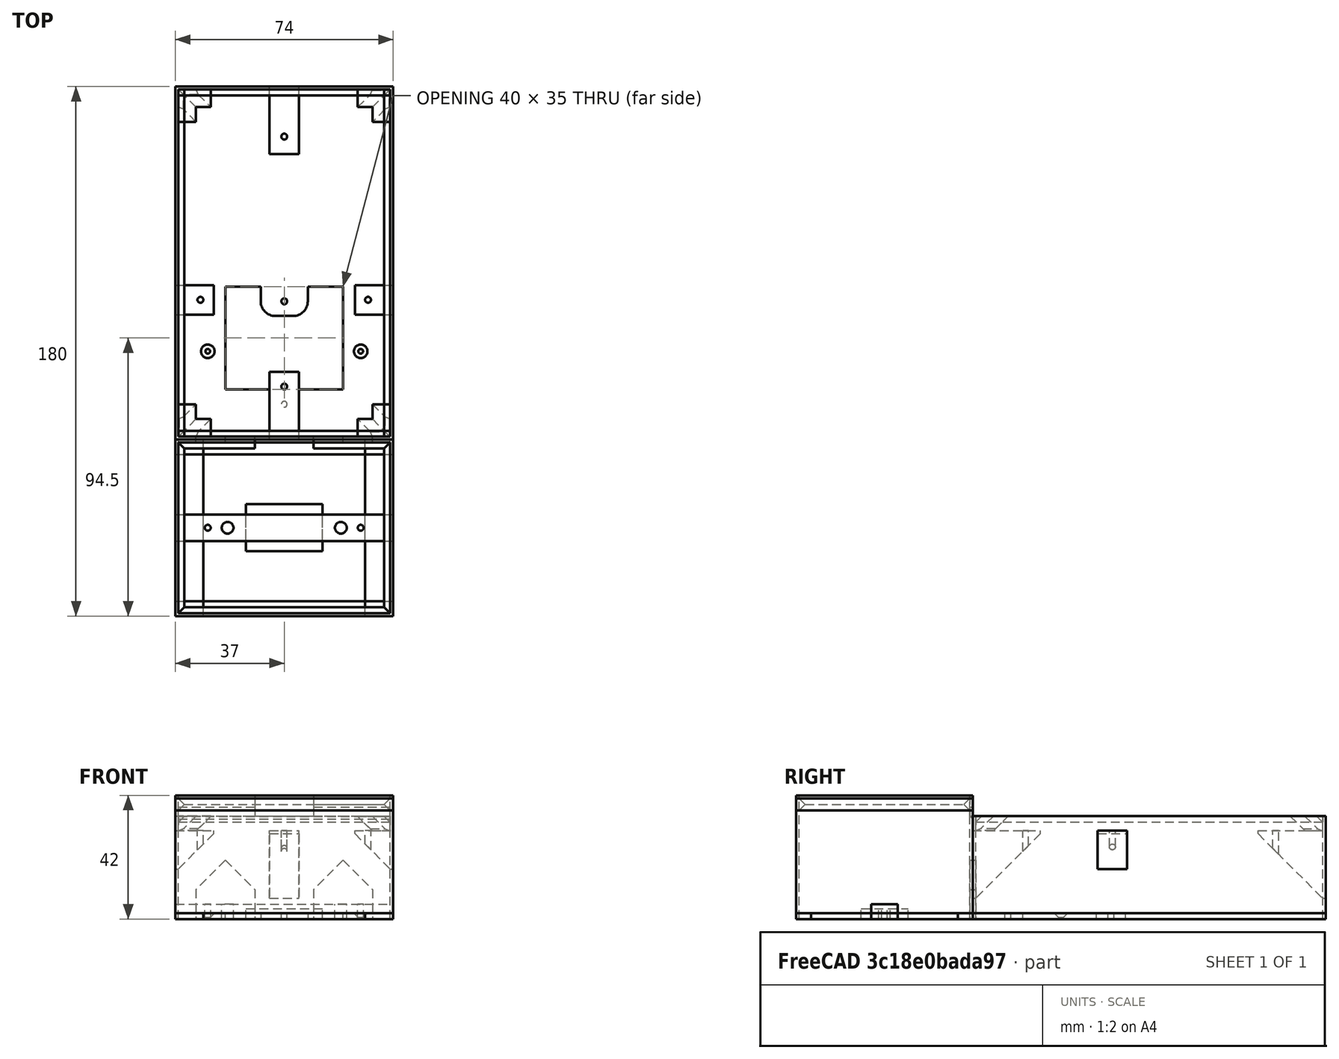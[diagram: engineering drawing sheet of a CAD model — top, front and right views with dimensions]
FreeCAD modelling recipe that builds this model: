
FCSTD DOCUMENT  (FreeCAD 0.16R)
Label: sonoff-T1-US-aufputz-und-Steckdose_v2.3
License: All rights reserved
LicenseURL: http://en.wikipedia.org/wiki/All_rights_reserved
objects: Part::Box×37, Part::Cut×30, Part::Chamfer×24, Part::Cylinder×12, Part::Fillet×1
note: 104 computed .brp shape members not serialized (recipe doc carries the construction recipe); baked Part::Feature solids carry a one-line shape summary decoded from their .brp

FEATURE [Part::Box] Box028  label="Cube023"
  Height = 2
  Length = 72
  Placement = pos=(1,1,33) rot=(0,0,1;0rad)
  Width = 2
FEATURE [Part::Chamfer] Chamfer009
  Base = -> Box028
  Edges = 1 edges r=1.99: [Edge11]
FEATURE [Part::Box] Box037  label="Cube028"
  Height = 3.5
  Length = 26
  Placement = pos=(24,-38,0) rot=(0,0,1;0rad)
  Width = 16
FEATURE [Part::Cylinder] Cylinder
  Angle = 360
  Height = 10
  Placement = pos=(17.75,-30,0) rot=(0,0,1;0rad)
  Radius = 2
FEATURE [Part::Cylinder] Cylinder001
  Angle = 360
  Height = 10
  Placement = pos=(56.25,-30,0) rot=(0,0,1;0rad)
  Radius = 2
FEATURE [Part::Box] Box038  label="Kragen Stecker"
  Height = 4.1
  Length = 74
  Placement = pos=(0,-60,0) rot=(0,0,1;0rad)
  Width = 60
FEATURE [Part::Box] Box039  label="Kragen Stecker Ausschnitt"
  Height = 4.1
  Length = 68
  Placement = pos=(3,-57,0) rot=(0,0,1;0rad)
  Width = 54
FEATURE [Part::Cut] Cut019
  Base = -> Box038
  Placement = pos=(0,0,36.9) rot=(0,0,1;0rad)
  Tool = -> Box039
FEATURE [Part::Chamfer] Chamfer021
  Base = -> Cut019
  Edges = 4 edges r=2: [Edge10,Edge11,Edge12,Edge13]
FEATURE [Part::Chamfer] Chamfer022  label="Kragen"
  Base = -> Chamfer021
  Edges = 4 edges r=2: [Edge26,Edge29,Edge31,Edge32]
FEATURE [Part::Box] Box045  label="Cube034"
  Height = 4
  Length = 72
  Placement = pos=(1,-1,34) rot=(0,0,1;0rad)
  Width = 1
FEATURE [Part::Chamfer] Chamfer027  label="Verstärkung"
  Base = -> Box045
  Edges = 1 edges r=0.99: [Edge9]
FEATURE [Part::Box] Box032  label="Basis Stecker"
  Height = 42
  Length = 74
  Placement = pos=(0,-60,0) rot=(0,0,1;0rad)
  Width = 60
FEATURE [Part::Box] Box033  label="Ausschnitt Stecker"
  Height = 42
  Length = 72
  Placement = pos=(1,-59,0) rot=(0,0,1;0rad)
  Width = 58
FEATURE [Part::Cut] Cut014
  Base = -> Box032
  Tool = -> Box033
FEATURE [Part::Box] Box  label="Basis"
  Height = 35
  Length = 74
  Width = 120
FEATURE [Part::Box] Box001  label="Ausschnitt"
  Height = 35
  Length = 72
  Placement = pos=(1,1,0) rot=(0,0,1;0rad)
  Width = 118
FEATURE [Part::Cut] Cut
  Base = -> Box
  Tool = -> Box001
FEATURE [Part::Box] Box014  label="Basis001"
  Height = 2
  Length = 74
  Width = 120
FEATURE [Part::Box] Box024  label="Cube019"
  Height = 5
  Length = 5
  Placement = pos=(63,109,30) rot=(0,0,1;0rad)
  Width = 5
FEATURE [Part::Box] Box025  label="Cube020"
  Height = 5
  Length = 11
  Placement = pos=(63,109,30) rot=(0,0,1;0rad)
  Width = 11
FEATURE [Part::Cut] Cut012
  Base = -> Box025
  Tool = -> Box024
FEATURE [Part::Chamfer] Chamfer004
  Base = -> Cut012
  Edges = 4 edges r=4.9: [Edge4,Edge5,Edge15,Edge16]
  Placement = pos=(-1,-1,0) rot=(0,0,1;0rad)
FEATURE [Part::Box] Box046  label="Cube035"
  Height = 2
  Length = 72
  Placement = pos=(1,1,33) rot=(0,0,1;0rad)
  Width = 2
FEATURE [Part::Box] Box029  label="Cube024"
  Height = 2
  Length = 2
  Placement = pos=(1,1,33) rot=(0,0,1;0rad)
  Width = 118
FEATURE [Part::Box] Box030  label="Cube025"
  Height = 2
  Length = 72
  Placement = pos=(1,117,33) rot=(0,0,1;0rad)
  Width = 2
FEATURE [Part::Box] Box031  label="Cube026"
  Height = 2
  Length = 2
  Placement = pos=(71,1,33) rot=(0,0,1;0rad)
  Width = 118
FEATURE [Part::Chamfer] Chamfer008
  Base = -> Box031
  Edges = 1 edges r=1.9: [Edge4]
FEATURE [Part::Chamfer] Chamfer028
  Base = -> Box030
  Edges = 1 edges r=1.9: [Edge9]
FEATURE [Part::Chamfer] Chamfer010
  Base = -> Box029
  Edges = 1 edges r=1.9: [Edge8]
FEATURE [Part::Chamfer] Chamfer011
  Base = -> Box046
  Edges = 1 edges r=1.9: [Edge11]
FEATURE [Part::Box] Box047  label="Cube036"
  Height = 5
  Length = 11
  Placement = pos=(63,109,30) rot=(0,0,1;0rad)
  Width = 11
FEATURE [Part::Box] Box048  label="Cube037"
  Height = 5
  Length = 5
  Placement = pos=(63,109,30) rot=(0,0,1;0rad)
  Width = 5
FEATURE [Part::Cut] Cut013
  Base = -> Box047
  Tool = -> Box048
FEATURE [Part::Chamfer] Chamfer012
  Base = -> Cut013
  Edges = 4 edges r=4.9: [Edge4,Edge5,Edge15,Edge16]
  Placement = pos=(121,45,0) rot=(0,0,1;1.5708rad)
FEATURE [Part::Chamfer] Chamfer013
  Base = -> Chamfer004
  Edges = 2 edges r=0.9: [Edge19,Edge23]
FEATURE [Part::Chamfer] Chamfer014
  Base = -> Chamfer012
  Edges = 2 edges r=0.9: [Edge19,Edge23]
FEATURE [Part::Box] Box034  label="Cube029"
  Height = 5
  Length = 5
  Placement = pos=(63,109,30) rot=(0,0,1;0rad)
  Width = 5
FEATURE [Part::Box] Box035  label="Cube030"
  Height = 5
  Length = 11
  Placement = pos=(63,109,30) rot=(0,0,1;0rad)
  Width = 11
FEATURE [Part::Cut] Cut020
  Base = -> Box035
  Tool = -> Box034
FEATURE [Part::Chamfer] Chamfer015
  Base = -> Cut020
  Edges = 4 edges r=4.9: [Edge4,Edge5,Edge15,Edge16]
  Placement = pos=(-1,-1,0) rot=(0,0,1;0rad)
FEATURE [Part::Chamfer] Chamfer016
  Base = -> Chamfer015
  Edges = 2 edges r=0.9: [Edge19,Edge23]
  Placement = pos=(74,120,0) rot=(0,0,1;3.14159rad)
FEATURE [Part::Box] Box049  label="Cube031"
  Height = 5
  Length = 5
  Placement = pos=(63,109,30) rot=(0,0,1;0rad)
  Width = 5
FEATURE [Part::Box] Box050  label="Cube032"
  Height = 5
  Length = 11
  Placement = pos=(63,109,30) rot=(0,0,1;0rad)
  Width = 11
FEATURE [Part::Cut] Cut015
  Base = -> Box050
  Tool = -> Box049
FEATURE [Part::Chamfer] Chamfer017
  Base = -> Cut015
  Edges = 4 edges r=4.9: [Edge4,Edge5,Edge15,Edge16]
  Placement = pos=(-1,-1,0) rot=(0,0,1;0rad)
FEATURE [Part::Chamfer] Chamfer018
  Base = -> Chamfer017
  Edges = 2 edges r=0.9: [Edge19,Edge23]
  Placement = pos=(-46,74,0) rot=(0,0,-1;1.5708rad)
FEATURE [Part::Box] Box051  label="Cube"
  Height = 13
  Length = 13
  Placement = pos=(0,42.5,17) rot=(0,0,1;0rad)
  Width = 10
FEATURE [Part::Box] Box052  label="Cube033"
  Height = 13
  Length = 13
  Placement = pos=(61,42.5,17) rot=(0,0,1;0rad)
  Width = 10
FEATURE [Part::Box] Box040  label="Cube038"
  Height = 23
  Length = 10
  Placement = pos=(32,0,7) rot=(0,0,1;0rad)
  Width = 23
FEATURE [Part::Box] Box041  label="Cube039"
  Height = 23
  Length = 10
  Placement = pos=(32,97,7) rot=(0,0,1;0rad)
  Width = 23
FEATURE [Part::Chamfer] Chamfer019
  Base = -> Box040
  Edges = 1 edges r=22: [Edge11]
FEATURE [Part::Chamfer] Chamfer020
  Base = -> Box041
  Edges = 1 edges r=22: [Edge9]
FEATURE [Part::Chamfer] Chamfer029
  Base = -> Box051
  Edges = 1 edges r=12: [Edge8]
FEATURE [Part::Chamfer] Chamfer030
  Base = -> Box052
  Edges = 1 edges r=12: [Edge4]
FEATURE [Part::Cylinder] Cylinder002
  Angle = 360
  Height = 40
  Placement = pos=(37,18,0) rot=(0,0,1;0rad)
  Radius = 1
FEATURE [Part::Cylinder] Cylinder003
  Angle = 360
  Height = 40
  Placement = pos=(37,103,0) rot=(0,0,1;0rad)
  Radius = 1
FEATURE [Part::Cylinder] Cylinder004
  Angle = 360
  Height = 40
  Placement = pos=(8.5,47.5,0) rot=(0,0,1;0rad)
  Radius = 1
FEATURE [Part::Cylinder] Cylinder005
  Angle = 360
  Height = 40
  Placement = pos=(65.5,47.5,0) rot=(0,0,1;0rad)
  Radius = 1
FEATURE [Part::Cut] Cut021
  Base = -> Chamfer019
  Tool = -> Cylinder002
FEATURE [Part::Cut] Cut022
  Base = -> Chamfer030
  Tool = -> Cylinder005
FEATURE [Part::Cut] Cut018
  Base = -> Chamfer029
  Tool = -> Cylinder004
FEATURE [Part::Cut] Cut023
  Base = -> Chamfer020
  Tool = -> Cylinder003
FEATURE [Part::Cylinder] Cylinder006
  Angle = 360
  Height = 10
  Placement = pos=(11,30,0) rot=(0,0,1;0rad)
  Radius = 0.8
FEATURE [Part::Cylinder] Cylinder007
  Angle = 360
  Height = 10
  Placement = pos=(63,30,0) rot=(0,0,1;0rad)
  Radius = 0.8
FEATURE [Part::Cut] Cut024
  Base = -> Box014
  Tool = -> Cylinder006
FEATURE [Part::Cut] Cut025
  Base = -> Cut024
  Tool = -> Cylinder007
FEATURE [Part::Chamfer] Chamfer
  Base = -> Cut025
  Edges = 1 edges r=1.5: [Edge11]
FEATURE [Part::Chamfer] Chamfer031
  Base = -> Chamfer
  Edges = 1 edges r=1.5: [Edge6]
FEATURE [Part::Box] Box053  label="Cube040"
  Height = 10
  Length = 40
  Placement = pos=(17,17,0) rot=(0,0,1;0rad)
  Width = 25
FEATURE [Part::Cylinder] Cylinder008
  Angle = 360
  Height = 10
  Placement = pos=(37,12,0) rot=(0,0,1;0rad)
  Radius = 1
FEATURE [Part::Cylinder] Cylinder009
  Angle = 360
  Height = 10
  Placement = pos=(37,47,0) rot=(0,0,1;0rad)
  Radius = 1
FEATURE [Part::Cut] Cut026
  Base = -> Chamfer031
  Tool = -> Box053
FEATURE [Part::Cut] Cut027
  Base = -> Cut026
  Tool = -> Cylinder008
FEATURE [Part::Cut] Cut028
  Base = -> Cut027
  Tool = -> Cylinder009
FEATURE [Part::Box] Box054  label="Cube041"
  Height = 20
  Length = 20
  Placement = pos=(7,-5,0) rot=(0,0,1;0rad)
  Width = 10
FEATURE [Part::Box] Box055  label="Cube042"
  Height = 20
  Length = 20
  Placement = pos=(47,-5,0) rot=(0,0,1;0rad)
  Width = 10
FEATURE [Part::Chamfer] Chamfer033
  Base = -> Box054
  Edges = 2 edges r=9.99: [Edge2,Edge6]
FEATURE [Part::Chamfer] Chamfer034
  Base = -> Box055
  Edges = 2 edges r=9.99: [Edge2,Edge6]
FEATURE [Part::Cut] Cut029
  Base = -> Cut
  Tool = -> Chamfer033
FEATURE [Part::Cut] Cut030
  Base = -> Cut029
  Tool = -> Chamfer033
FEATURE [Part::Cut] Cut031
  Base = -> Cut030
  Tool = -> Chamfer034
FEATURE [Part::Cut] Cut032
  Base = -> Cut014
  Tool = -> Chamfer033
FEATURE [Part::Cut] Cut033
  Base = -> Cut032
  Tool = -> Chamfer034
FEATURE [Part::Box] Box056  label="Cube043"
  Height = 10
  Length = 20
  Placement = pos=(27,-5,35) rot=(0,0,1;0rad)
  Width = 10
FEATURE [Part::Cut] Cut034
  Base = -> Chamfer022
  Tool = -> Box056
FEATURE [Part::Cut] Cut035
  Base = -> Cut033
  Tool = -> Box056
FEATURE [Part::Cut] Cut036
  Base = -> Chamfer027
  Tool = -> Box056
FEATURE [Part::Box] Box058  label="Cube045"
  Height = 5
  Length = 74
  Placement = pos=(0,-34.5,0) rot=(0,0,1;0rad)
  Width = 9
FEATURE [Part::Box] Box059  label="Cube046"
  Height = 2
  Length = 9.5
  Placement = pos=(0,-60,0) rot=(0,0,1;0rad)
  Width = 60
FEATURE [Part::Box] Box060  label="Cube047"
  Height = 2
  Length = 9.5
  Placement = pos=(64.5,-60,0) rot=(0,0,1;0rad)
  Width = 60
FEATURE [Part::Box] Box061  label="Cube048"
  Height = 2
  Length = 74
  Placement = pos=(0,-5,0) rot=(0,0,1;0rad)
  Width = 5
FEATURE [Part::Box] Box062  label="Cube049"
  Height = 2
  Length = 74
  Placement = pos=(0,-60,0) rot=(0,0,1;0rad)
  Width = 5
FEATURE [Part::Cylinder] Cylinder010
  Angle = 360
  Height = 10
  Placement = pos=(11,-30,0) rot=(0,0,1;0rad)
  Radius = 1
FEATURE [Part::Cylinder] Cylinder011
  Angle = 360
  Height = 10
  Placement = pos=(63,-30,0) rot=(0,0,1;0rad)
  Radius = 1
FEATURE [Part::Cut] Cut037
  Base = -> Box058
  Tool = -> Cylinder
FEATURE [Part::Cut] Cut038
  Base = -> Cut037
  Tool = -> Cylinder001
FEATURE [Part::Cut] Cut039
  Base = -> Cut038
  Tool = -> Cylinder010
FEATURE [Part::Cut] Cut040
  Base = -> Cut039
  Tool = -> Cylinder011
FEATURE [Part::Box] Box063  label="Cube050"
  Height = 10
  Length = 12
  Placement = pos=(17,40,0) rot=(0,0,1;0rad)
  Width = 12
FEATURE [Part::Box] Box064  label="Cube051"
  Height = 10
  Length = 12
  Placement = pos=(45,40,0) rot=(0,0,1;0rad)
  Width = 12
FEATURE [Part::Cut] Cut041
  Base = -> Cut028
  Tool = -> Box063
FEATURE [Part::Cut] Cut042
  Base = -> Cut041
  Tool = -> Box064
FEATURE [Part::Fillet] Fillet
  Base = -> Cut042
  Edges = 2 edges r=5: [Edge44,Edge46]
